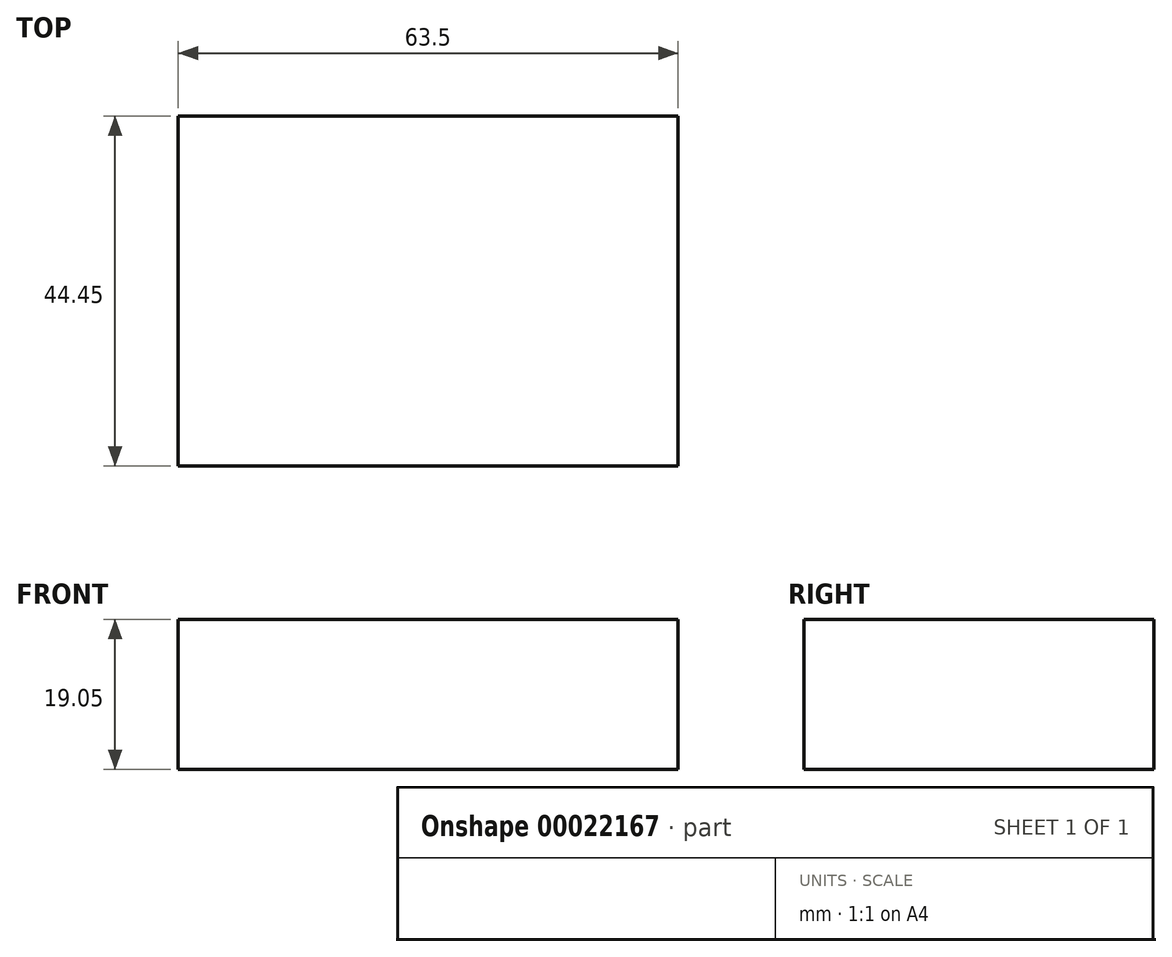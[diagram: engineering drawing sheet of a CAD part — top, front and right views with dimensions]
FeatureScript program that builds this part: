
annotation { "Feature Type Name" : "Feature", "Feature Type Description" : "" }
export const myFeature = defineFeature(function(context is Context, id is Id, definition is map)
    precondition{}
    {
        {
            var Q0;
            Q0=qCreatedBy(makeId("Front.planeOp"),FACE);
            var sketch = newSketch(context, id + "F0", { "sketchPlane" : qUnion([Q0])});
            skLineSegment(sketch, "E0", {"start": v(-61.38, -19.05) * mm, "end": v(-61.38, 0) * mm});
            skLineSegment(sketch, "E1", {"start": v(-61.38, 0) * mm, "end": v(2.12, 0) * mm});
            skLineSegment(sketch, "E2", {"start": v(2.12, 0) * mm, "end": v(2.12, -19.05) * mm});
            skLineSegment(sketch, "E3", {"start": v(2.12, -19.05) * mm, "end": v(-61.38, -19.05) * mm});
            skSolve(sketch);
        }
        {
            var Q0;
            Q0 = qSketchRegion(id + "F0", true);
            extrude(context, id + "F1", {"entities" : qUnion([Q0]), "depth" : 44.45 * mm});
        }
    });
